# Revit family: Illusion Soft LED - Ceiling Based
name_source: partatom
category: Lighting Fixtures
revit_build: Autodesk Revit Architecture 2014 (Build: 20140709_2115(x64)
units: mm (PartAtom-declared; Revit-internal decimal feet)

## types (2) — shared parameters
Apparent Load = 240 VA
ArticleNumber = See URL hyperlink
AssetType = Moveable/Fixed
BSAB 96 = SNB.2
BallastsCELMAEnergyEfficiencyIndex = Class A1/A2
CCSClassCode = UAC
CCSClassName = Belysningsarmatur
CCSTopnode = L
Cassette = Riegens_Steel_Powder coated white RAL901025
Cassette Depth = 572 mm
Cassette Width = 572 mm
Clearance Zones = Yes
Clearance Zones Offset = 60 mm
Color Filter = 16777215
Colour = White
ControlGearPosition = Integrated
Description = 70-80-35 General Lighting Systems
Dimming Lamp Color Temperature Shift = <None>
DocumentReference = See URL hyperlink
Documentation = See URL hyperlink
Finish = Powder coated
Frame = Riegens_Steel_Powder coated white RAL901025
Glass = Riegens_Glass_opal
Glass Thickness = 2 mm
HasProtectiveEarth = TRUE
Height 1 = 126 mm
Height 2 = 85 mm
IP_Code = IP20
IfcExportAs = IfcLightFixtureType'
IfcExportType = NOTDEFINED'
InsulationStandardClass = Class 1
InternalFuse = Only required in emergency versions
LampColourRenderingIndex = Ra>80
LampRating = 35W
LampType = LED
LightFixtureMountingType = Recessed
LightFixturePlacingType = Ceiling
LightSource = LED 3000K / 4000K
LuminairePowerFactor = >0,9
LuminaireType = Recessed Direct LED Luminaire
Manufacturer = Riegens A/S
ManufacturerURL = www.riegens.com
Material = Steel and Acrylic (PMMA)
NominalVoltage = 220-240V
Optic = Micro-prism lens
PhaseReference = IEC recommendations
Photometric Web File = Illusion Soft 600x600 TL 35W LED 4000K.ies
PhotometricPerformance = In accordance with BS EN 13032-1
ProductInformation = http://riegens.co.uk
Shape = Square
Size = 600 x 600 mm
Tilt Angle = 90.00°
TotalWattage = Max. 36W
URL = http://riegens.co.uk
Uniclass 1.4 = JY73
Uniclass2 = Pr_70_70_49_43 Light-Emitting Diode (LED) Luminaires
Version = v.1.0

## per-type parameters (varying)
| type | BIMObjectName | Frame Depth | Frame Width | Transformer |
| Illusion Soft LED 600x600 C | Illusion Soft LED 600x600 C.rfa | 599 mm | 599 mm | Riegens_Aluminum |
| Illusion Soft LED 600x600 T/L | Illusion Soft LED 600x600 T/L.rfa | 595 mm | 595 mm | Riegens_Glass_opal |

note: column(s) folded — value = type name in every type: Model, ModelReference
